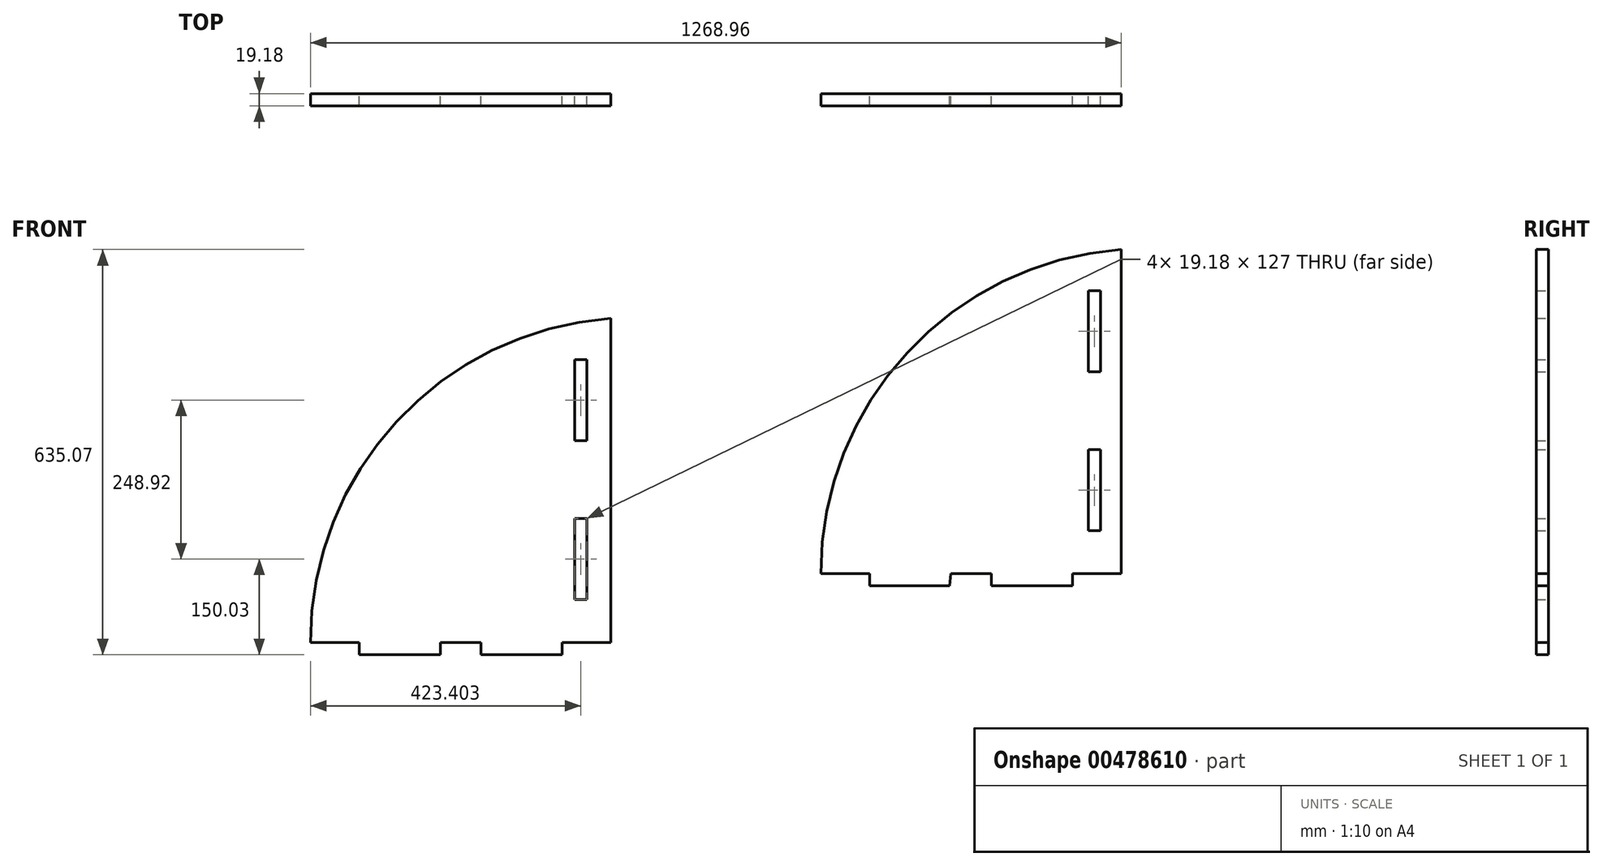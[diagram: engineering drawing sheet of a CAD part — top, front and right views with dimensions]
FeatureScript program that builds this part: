
annotation { "Feature Type Name" : "Feature", "Feature Type Description" : "" }
export const myFeature = defineFeature(function(context is Context, id is Id, definition is map)
    precondition{}
    {
        {
            var Q0;
            Q0=qCreatedBy(makeId("Front.planeOp"),FACE);
            var sketch = newSketch(context, id + "F0", { "sketchPlane" : qUnion([Q0])});
            skLineSegment(sketch, "E0", {"start": v(121.9, 333.9) * mm, "end": v(121.9, -174.1) * mm});
            skArc(sketch, "E1", {"start": v(121.9, 333.9) * mm, "mid": v(-212.93, 172.28) * mm, "end": v(-348, -174.1) * mm});
            skLineSegment(sketch, "E2", {"start": v(-348, -174.1) * mm, "end": v(-271.8, -174.1) * mm});
            skLineSegment(sketch, "E3", {"start": v(-144.8, -174.1) * mm, "end": v(-81.3, -174.1) * mm});
            skLineSegment(sketch, "E4", {"start": v(45.7, -174.1) * mm, "end": v(121.9, -174.1) * mm});
            skLineSegment(sketch, "E5", {"start": v(70.37, 142.17) * mm, "end": v(89.55, 142.17) * mm});
            skLineSegment(sketch, "E6", {"start": v(89.55, 142.17) * mm, "end": v(89.55, 269.17) * mm});
            skLineSegment(sketch, "E7", {"start": v(70.37, 142.17) * mm, "end": v(70.37, 269.17) * mm});
            skLineSegment(sketch, "E8", {"start": v(89.55, 269.17) * mm, "end": v(70.37, 269.17) * mm});
            skLineSegment(sketch, "E9", {"start": v(70.37, 20.25) * mm, "end": v(70.37, -106.75) * mm});
            skLineSegment(sketch, "E10", {"start": v(70.37, -106.75) * mm, "end": v(89.55, -106.75) * mm});
            skLineSegment(sketch, "E11", {"start": v(89.55, -106.75) * mm, "end": v(89.55, 20.25) * mm});
            skLineSegment(sketch, "E12", {"start": v(70.37, 20.25) * mm, "end": v(89.55, 20.25) * mm});
            skLineSegment(sketch, "E13", {"start": v(-271.8, -174.1) * mm, "end": v(-144.8, -174.1) * mm});
            skLineSegment(sketch, "E14", {"start": v(-81.3, -174.1) * mm, "end": v(45.7, -174.1) * mm});
            skLineSegment(sketch, "E15", {"start": v(-271.8, -174.1) * mm, "end": v(-271.8, -193.28) * mm});
            skLineSegment(sketch, "E16", {"start": v(-271.8, -193.28) * mm, "end": v(-146.83, -193.28) * mm});
            skLineSegment(sketch, "E17", {"start": v(-146.83, -193.28) * mm, "end": v(-144.8, -174.1) * mm});
            skLineSegment(sketch, "E18", {"start": v(-81.3, -174.1) * mm, "end": v(-81.3, -193.27) * mm});
            skLineSegment(sketch, "E19", {"start": v(-81.3, -193.27) * mm, "end": v(46.05, -193.27) * mm});
            skLineSegment(sketch, "E20", {"start": v(46.05, -193.27) * mm, "end": v(45.7, -174.1) * mm});
            skLineSegment(sketch, "E21", {"start": v(-677.16, 226) * mm, "end": v(-677.16, -282) * mm});
            skArc(sketch, "E22", {"start": v(-677.16, 226) * mm, "mid": v(-1011.99, 64.4) * mm, "end": v(-1147.06, -282) * mm});
            skLineSegment(sketch, "E23", {"start": v(-1147.06, -282) * mm, "end": v(-1070.86, -282) * mm});
            skLineSegment(sketch, "E24", {"start": v(-943.86, -282) * mm, "end": v(-880.36, -282) * mm});
            skLineSegment(sketch, "E25", {"start": v(-753.36, -282) * mm, "end": v(-677.16, -282) * mm});
            skLineSegment(sketch, "E26", {"start": v(-733.26, 34.28) * mm, "end": v(-714.08, 34.28) * mm});
            skLineSegment(sketch, "E27", {"start": v(-714.08, 34.28) * mm, "end": v(-714.08, 161.28) * mm});
            skLineSegment(sketch, "E28", {"start": v(-733.26, 34.28) * mm, "end": v(-733.26, 161.28) * mm});
            skLineSegment(sketch, "E29", {"start": v(-714.08, 161.28) * mm, "end": v(-733.26, 161.28) * mm});
            skLineSegment(sketch, "E30", {"start": v(-733.26, -87.64) * mm, "end": v(-733.26, -214.64) * mm});
            skLineSegment(sketch, "E31", {"start": v(-733.26, -214.64) * mm, "end": v(-714.08, -214.64) * mm});
            skLineSegment(sketch, "E32", {"start": v(-714.08, -214.64) * mm, "end": v(-714.08, -87.64) * mm});
            skLineSegment(sketch, "E33", {"start": v(-733.26, -87.64) * mm, "end": v(-714.08, -87.64) * mm});
            skLineSegment(sketch, "E34", {"start": v(-1070.86, -282) * mm, "end": v(-1070.86, -301.17) * mm});
            skLineSegment(sketch, "E35", {"start": v(-1070.86, -301.17) * mm, "end": v(-943.86, -301.17) * mm});
            skLineSegment(sketch, "E36", {"start": v(-943.86, -301.17) * mm, "end": v(-943.86, -282) * mm});
            skLineSegment(sketch, "E37", {"start": v(-880.36, -282) * mm, "end": v(-880.36, -301.17) * mm});
            skLineSegment(sketch, "E38", {"start": v(-880.36, -301.17) * mm, "end": v(-753.36, -301.17) * mm});
            skLineSegment(sketch, "E39", {"start": v(-753.36, -301.17) * mm, "end": v(-753.36, -282) * mm});
            skSolve(sketch);
        }
        {
            var Q0;
            Q0=qSketchRegion(id+"F0",true);
            extrude(context, id + "F1", {"entities" : qUnion([Q0]), "depth" : 19.18 * mm, "offsetDistance" : 25.4 * mm});
        }
    });
